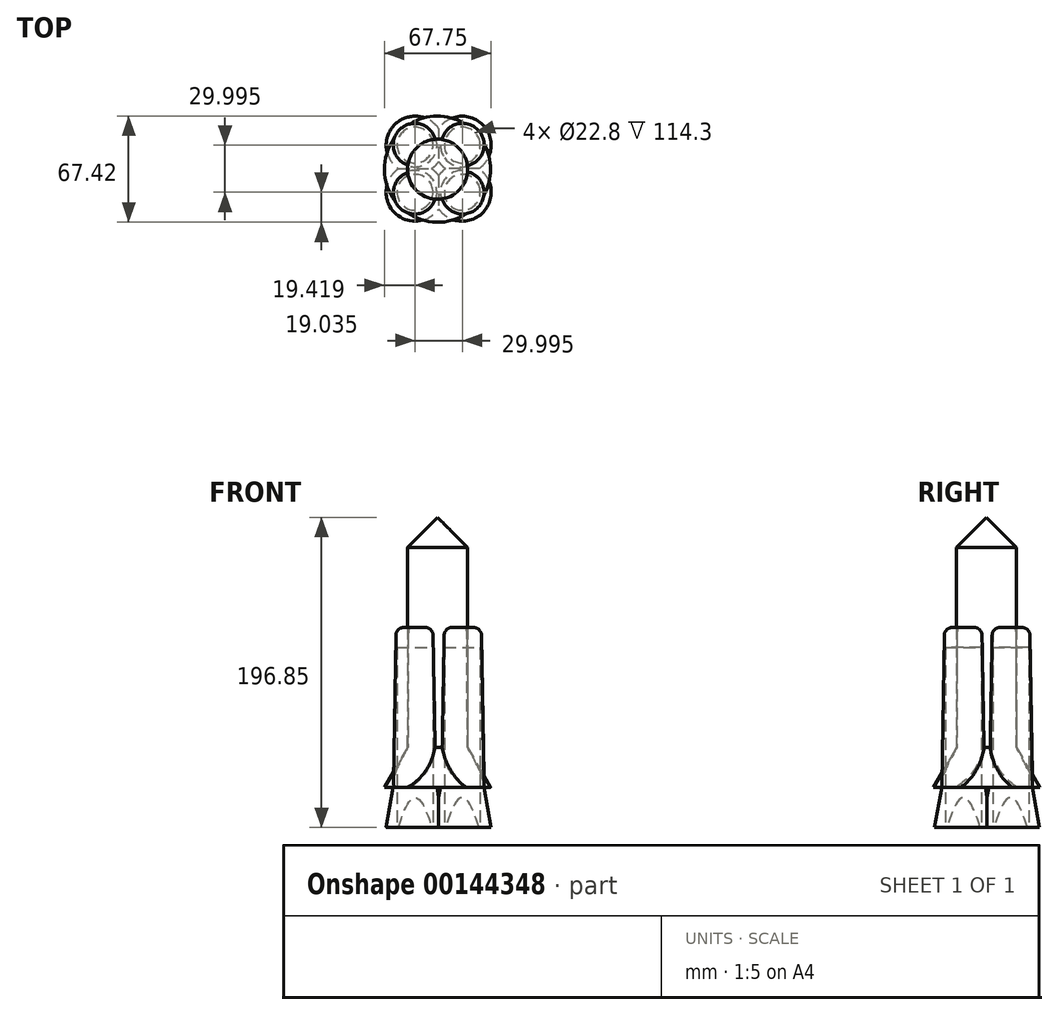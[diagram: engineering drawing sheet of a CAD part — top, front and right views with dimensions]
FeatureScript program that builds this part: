
annotation { "Feature Type Name" : "Feature", "Feature Type Description" : "" }
export const myFeature = defineFeature(function(context is Context, id is Id, definition is map)
    precondition{}
    {
        {
            var Q0;
            Q0=qCreatedBy(makeId("Top.planeOp"),FACE);
            var sketch = newSketch(context, id + "F0", { "sketchPlane" : qUnion([Q0])});
            skCircle(sketch, "E0", {"center": v(0, 0) * mm, "radius": 19.05 * mm});
            skSolve(sketch);
        }
        {
            var Q0;
            Q0 = qSketchRegion(id + "F0", true);
            extrude(context, id + "F1", {"entities" : qUnion([Q0]), "depth" : 127 * mm});
        }
        {
            var Q0;
            Q0=makeQuery(id+"F1.opExtrude","CAP_FACE",FACE,{"disambiguationData":[OSD([sQuery(id+"F0.wireOp",EDGE,"E0")])],"isStart":false});
            var sketch = newSketch(context, id + "F2", { "sketchPlane" : qUnion([Q0])});
            skCircle(sketch, "E1", {"center": v(0, 0) * mm, "radius": 19.05 * mm});
            skSolve(sketch);
        }
        {
            var Q0;
            Q0=makeQuery(id+"F2.imprint","IMPRINT",FACE,{"disambiguationData":[TD([[makeQuery(id+"F2.imprint","IMPRINT",EDGE,{"derivedFrom":sQuery(id+"F2.wireOp",EDGE,"E1")}),1.0]])]});
            extrude(context, id + "F3", {"entities" : qUnion([Q0]), "operationType" : NewBodyOperationType.ADD, "depth" : 1270 * mm, "hasDraft" : true, "draftAngle" : 45 * degree, "draftPullDirection" : true});
        }
        {
            var Q0;
            Q0=makeQuery(id+"F1.opExtrude","CAP_FACE",FACE,{"disambiguationData":[OSD([sQuery(id+"F0.wireOp",EDGE,"E0")])],"isStart":true});
            extrude(context, id + "F4", {"entities" : qUnion([Q0]), "operationType" : NewBodyOperationType.ADD, "depth" : 25.4 * mm, "hasDraft" : true, "draftAngle" : 30 * degree});
        }
        {
            var Q0;
            Q0=makeQuery(id+"F4.opExtrude","CAP_FACE",FACE,{"disambiguationData":[OSD([sQuery(id+"F0.wireOp",EDGE,"E0")])],"isStart":false});
            var sketch = newSketch(context, id + "F5", { "sketchPlane" : qUnion([Q0])});
            skCircle(sketch, "E2", {"center": v(-14.3, 14.67) * mm, "radius": 13.86 * mm});
            skCircle(sketch, "E3", {"center": v(-14.3, -15.32) * mm, "radius": 13.86 * mm});
            skCircle(sketch, "E4", {"center": v(15.7, -15.32) * mm, "radius": 13.86 * mm});
            skLineSegment(sketch, "E5", {"start": v(-14.3, 14.67) * mm, "end": v(-14.3, -15.32) * mm, "construction": true});
            skLineSegment(sketch, "E6", {"start": v(-14.3, -15.32) * mm, "end": v(15.7, -15.32) * mm, "construction": true});
            skLineSegment(sketch, "E7", {"start": v(15.7, -15.32) * mm, "end": v(15.7, 14.67) * mm, "construction": true});
            skLineSegment(sketch, "E8", {"start": v(15.7, 14.67) * mm, "end": v(-14.3, 14.67) * mm, "construction": true});
            skCircle(sketch, "E9", {"center": v(15.7, 14.67) * mm, "radius": 13.86 * mm});
            skLineSegment(sketch, "E10", {"start": v(0, 14.67) * mm, "end": v(0, 0) * mm, "construction": true});
            skLineSegment(sketch, "E11", {"start": v(0, 0) * mm, "end": v(-14.3, 0) * mm, "construction": true});
            skSolve(sketch);
        }
        {
            var Q0;
            Q0=makeQuery(id+"F5.imprint","IMPRINT",FACE,{"disambiguationData":[TD([[makeQuery(id+"F5.imprint","IMPRINT",EDGE,{"derivedFrom":sQuery(id+"F5.wireOp",EDGE,"E3")}),1.0]])]});
            var Q1;
            Q1=makeQuery(id+"F5.imprint","IMPRINT",FACE,{"disambiguationData":[TD([[makeQuery(id+"F5.imprint","IMPRINT",EDGE,{"derivedFrom":sQuery(id+"F5.wireOp",EDGE,"E4")}),1.0]])]});
            var Q2;
            Q2=makeQuery(id+"F5.imprint","IMPRINT",FACE,{"disambiguationData":[TD([[makeQuery(id+"F5.imprint","IMPRINT",EDGE,{"derivedFrom":sQuery(id+"F5.wireOp",EDGE,"E2")}),1.0]])]});
            var Q3;
            Q3=makeQuery(id+"F5.imprint","IMPRINT",FACE,{"disambiguationData":[TD([[makeQuery(id+"F5.imprint","IMPRINT",EDGE,{"derivedFrom":sQuery(id+"F5.wireOp",EDGE,"E9")}),1.0]])]});
            extrude(context, id + "F6", {"entities" : qUnion([Q0, Q1, Q2, Q3]), "operationType" : NewBodyOperationType.ADD, "oppositeDirection" : true, "depth" : 101.6 * mm, "hasDraft" : true, "draftAngle" : 1 * degree, "draftPullDirection" : true});
        }
        {
            var Q0;
            Q0=makeQuery(id+"F6.opExtrude","CAP_EDGE",EDGE,{"disambiguationData":[OSD([sQuery(id+"F5.wireOp",EDGE,"E4")])],"isStart":false});
            var Q1;
            Q1=makeQuery(id+"F6.opExtrude","CAP_EDGE",EDGE,{"disambiguationData":[OSD([sQuery(id+"F5.wireOp",EDGE,"E3")])],"isStart":false});
            var Q2;
            Q2=makeQuery(id+"F6.opExtrude","CAP_EDGE",EDGE,{"disambiguationData":[OSD([sQuery(id+"F5.wireOp",EDGE,"E2")])],"isStart":false});
            var Q3;
            Q3=makeQuery(id+"F6.opExtrude","CAP_EDGE",EDGE,{"disambiguationData":[OSD([sQuery(id+"F5.wireOp",EDGE,"E9")])],"isStart":false});
            fillet(context, id + "F7", {"entities" : qUnion([Q0, Q1, Q2, Q3]), "radius" : 5.08 * mm, "tangentPropagation" : true, "allowEdgeOverflow" : false});
        }
        {
            var Q0;
            Q0 = qSketchRegion(id + "F5", true);
            extrude(context, id + "F8", {"entities" : qUnion([Q0]), "operationType" : NewBodyOperationType.ADD, "depth" : 25.4 * mm, "hasDraft" : true, "draftAngle" : 10 * degree});
        }
        {
            var Q0;
            Q0=makeQuery(id+"F8.boolean.opBoolean","MERGE",FACE,{"derivedFrom":[makeQuery(id+"F8.opExtrude","CAP_FACE",FACE,{"disambiguationData":[OSD([sQuery(id+"F5.wireOp",EDGE,"E2")])],"isStart":false}),makeQuery(id+"F8.opExtrude","CAP_FACE",FACE,{"disambiguationData":[OSD([sQuery(id+"F5.wireOp",EDGE,"E3")])],"isStart":false}),makeQuery(id+"F8.opExtrude","CAP_FACE",FACE,{"disambiguationData":[OSD([sQuery(id+"F5.wireOp",EDGE,"E4")])],"isStart":false}),makeQuery(id+"F8.opExtrude","CAP_FACE",FACE,{"disambiguationData":[OSD([sQuery(id+"F5.wireOp",EDGE,"E9")])],"isStart":false})]});
            var sketch = newSketch(context, id + "F9", { "sketchPlane" : qUnion([Q0])});
            skCircle(sketch, "E12", {"center": v(-14.3, -15.32) * mm, "radius": 11.4 * mm});
            skCircle(sketch, "E13", {"center": v(-14.3, 14.67) * mm, "radius": 11.4 * mm});
            skCircle(sketch, "E14", {"center": v(15.7, 14.67) * mm, "radius": 11.4 * mm});
            skCircle(sketch, "E15", {"center": v(15.7, -15.32) * mm, "radius": 11.4 * mm});
            skSolve(sketch);
        }
        {
            var Q0;
            Q0 = qSketchRegion(id + "F9", true);
            extrude(context, id + "F10", {"entities" : qUnion([Q0]), "operationType" : NewBodyOperationType.REMOVE, "oppositeDirection" : true, "depth" : 114.3 * mm});
        }
    });
